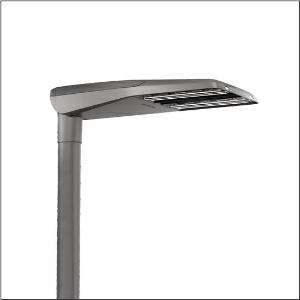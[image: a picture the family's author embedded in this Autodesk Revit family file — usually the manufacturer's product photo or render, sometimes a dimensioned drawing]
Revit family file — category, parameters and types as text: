
# Revit family: streetlight_sl_11_iq_midi___pc-r_5xc3f41e08me_ca65
name_source: partatom
category: Lighting Fixtures
units: mm (PartAtom-declared; Revit-internal decimal feet)

## family parameters
Cut with Voids When Loaded = No
Host = Face
Light Source = No
Part Type = Normal
Room Calculation Point = No
Round Connector Dimension = Use Diameter
Shared = No

## types (1)
- --- (1 x LED, 16220 lm, 124.7 W, 4000K)
    Apparent Load = 125 VA
    CIE Flux Codes = 37 73 96 100 100
    Color Rendering = 70
    Color Temperature = 4000K
    Default Elevation = 1800 mm
    Description = Streetlight SL 11 iQ midi, mast luminaire, primary light control with 3 zone facetted reflector, of plastic, silver coated, highly specular, primary optical cover: cover, of PMMA, transparent, light distribution: PC-R, light emission: direct distribution, primary light characteristic: asymmetric, right, installation type: post-top, side-entry, LED, High Power LED, rated luminous flux: 16.220lm, luminous efficacy: 130lm/W, light colour: 740, colour temperature: 4000K, control: optimised constant luminous flux control (CLO 2.0), Desk-Remote (wireless, voltage-free reading and setting of iQ features in the workshop via application-optimized NFC function/RFID function), Light-Fading, Smart-Wire, Night-Set, Lumen-Switch, Temp-Guard, Auto-Match, with cable H07RN-F 5x 1.5mm², mains connection: 230..240V, AC, 50/60Hz, connection cable pre-assembled, cable length: 12,5m, start of lifetime: 125W, end of service life: 132W, reduction: 57W, luminaire housing, of diecast aluminium, powder-coated, Siteco® metallic grey (DB 702S), please order mast flange separately, inclination adjustable without tools: 0°, 5°, 10°, 15° (post-top) | 0°, -5°, -10°, -15° (side-entry), sealing non-destructively replaceable, multi-level sealing system, length: 780mm, width: 376mm, height: 118mm, mast flange for spigot size: 42mm (side-entry): 5XC10008XM4, 60/48mm (side-entry/post-top): 5XC10108XM2, 76/60mm (side-entry/post-top): 5XC10108XM1, equipment: Power, protection rating (complete): IP66, insulation class (complete): insulation class II (safety insulation), certification: CE, ENEC, VDE, impact resistance: IK09, permissible operating ambient temperature for outdoor applications: -25..+50°C, standard-compliant lighting for roads and squares, Environmental Product Declaration (EPD) tested and certified by an independent institute, packaging unit: 1 piece

Light Distribution: PC-R
    Height = 118 mm
    Lamp = 1 x LED
    Lamp Light Flux = 16220 lm
    Lamp Power = 124.7 W
    Lamp count = 1
    Length = 780 mm
    Luminous efficacy = 130 lm/W
    Manufacturer = Siteco
    ModVariant = No
    Model = 5XC3F41E08ME
    Number of Poles = 1
    OnlyDefault = Yes
    Power Factor = 1
    Product Name = Streetlight SL 11 iQ midi | PC-R
    Product group = mast luminaire | pylon top
    ProductGroupID = 6100
    Protection Class = Protection class II
    Protection Degree = IP 66
    RLX_Detail_Level = 1
    RLX_Emergency_Light_Flux = 0 lm
    RLX_Emergency_Type = 0
    RLX_Emergency_Type_DB = No
    RlxData = <blob elided: 74557 chars, md5=70a6a7ed>
    Socket = socket
    Standby Power = 0 W
    System Light Flux = 16220 lm
    System Power = 125 W
    Type Comments = factory setting: luminous flux: 100 % | dim-lin: 254 | 557 mA
    Type Image = l_1005960.jpg
    URL = http://relux.com
    VarID = @adj_149123
    Voltage = 0 V
    Weight = 0.00 kg
    Width = 376 mm

## geometry (parser evidence)
native form markers: Blend x4, Sweep x11
no freeform markers — native parametric forms only
